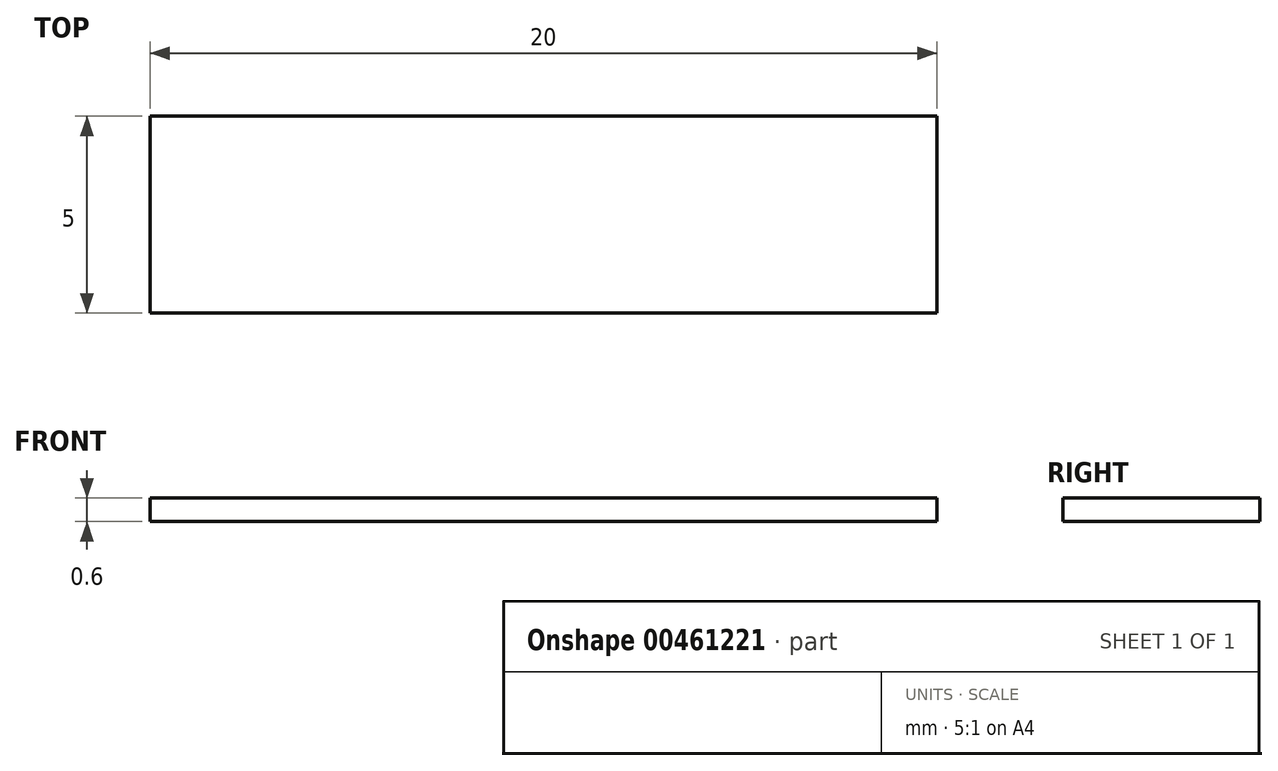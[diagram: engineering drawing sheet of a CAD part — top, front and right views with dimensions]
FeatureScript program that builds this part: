
annotation { "Feature Type Name" : "Feature", "Feature Type Description" : "" }
export const myFeature = defineFeature(function(context is Context, id is Id, definition is map)
    precondition{}
    {
        {
            var Q0;
            Q0=qCreatedBy(makeId("Top.planeOp"),FACE);
            var sketch = newSketch(context, id + "F0", { "sketchPlane" : qUnion([Q0])});
            skLineSegment(sketch, "E0.bottom", {"start": v(10, 2.5) * mm, "end": v(-10, 2.5) * mm});
            skLineSegment(sketch, "E0.top", {"start": v(10, -2.5) * mm, "end": v(-10, -2.5) * mm});
            skLineSegment(sketch, "E0.left", {"start": v(10, 2.5) * mm, "end": v(10, -2.5) * mm});
            skLineSegment(sketch, "E0.right", {"start": v(-10, 2.5) * mm, "end": v(-10, -2.5) * mm});
            skPoint(sketch, "E0.middle", {"position": v(0, 0) * mm});
            skSolve(sketch);
        }
        {
            var Q0;
            Q0=makeQuery(id+"F0.imprint","IMPRINT",FACE,{"disambiguationData":[TD([[makeQuery(id+"F0.imprint","IMPRINT",EDGE,{"derivedFrom":sQuery(id+"F0.wireOp",EDGE,"E0.bottom")}),1.0]])]});
            extrude(context, id + "F1", {"entities" : qUnion([Q0]), "depth" : .6 * mm});
        }
    });
